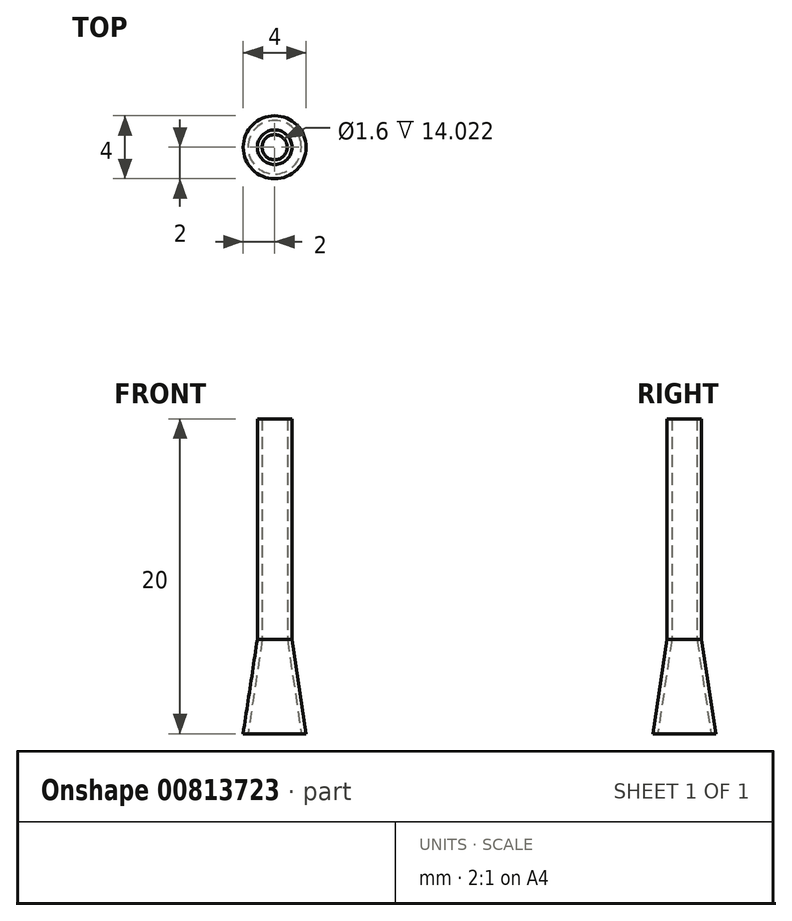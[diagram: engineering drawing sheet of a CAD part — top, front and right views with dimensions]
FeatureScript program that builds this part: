
annotation { "Feature Type Name" : "Feature", "Feature Type Description" : "" }
export const myFeature = defineFeature(function(context is Context, id is Id, definition is map)
    precondition{}
    {
        {
            var Q0;
            Q0=qCreatedBy(makeId("Front.planeOp"),FACE);
            var sketch = newSketch(context, id + "F0", { "sketchPlane" : qUnion([Q0])});
            skLineSegment(sketch, "E0", {"start": v(-1.7, 0) * mm, "end": v(-2, 0) * mm});
            skLineSegment(sketch, "E1", {"start": v(-2, 0) * mm, "end": v(-1.1, 6) * mm});
            skLineSegment(sketch, "E2", {"start": v(-1.1, 6) * mm, "end": v(-1.1, 20) * mm});
            skLineSegment(sketch, "E3", {"start": v(-1.1, 20) * mm, "end": v(-0.8, 20) * mm});
            skLineSegment(sketch, "E4", {"start": v(-0.8, 20) * mm, "end": v(-0.8, 5.98) * mm});
            skLineSegment(sketch, "E5", {"start": v(-1.7, 0) * mm, "end": v(-0.8, 5.98) * mm});
            skLineSegment(sketch, "E6", {"start": v(0, 0) * mm, "end": v(0, 11.66) * mm, "construction": true});
            skSolve(sketch);
        }
        {
            var Q0;
            Q0 = qSketchRegion(id + "F0", true);
            var Q1;
            Q1=sQuery(id+"F0.wireOp",EDGE,"E6");
            revolve(context, id + "F1", {"surfaceOperationType" : NewSurfaceOperationType.NEW, "entities" : qUnion([Q0]), "axis" : qUnion([Q1]), "revolveType" : RevolveType.FULL});
        }
    });
